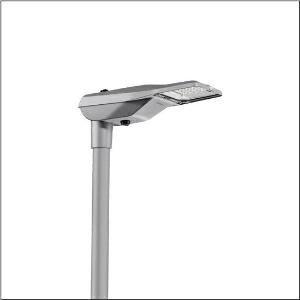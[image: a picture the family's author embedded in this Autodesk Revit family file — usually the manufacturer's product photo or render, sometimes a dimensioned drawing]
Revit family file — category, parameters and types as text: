
# Revit family: streetlight_sl_21_micro___st1_5a_5xe1p43t08db_e62a
name_source: partatom
category: Lighting Fixtures
units: mm (PartAtom-declared; Revit-internal decimal feet)

## family parameters
Cut with Voids When Loaded = No
Host = Face
Light Source = No
Part Type = Normal
Room Calculation Point = No
Round Connector Dimension = Use Diameter
Shared = No

## types (1)
- --- (1 x LED, 5230 lm, 39.1 W, 4000K)
    Apparent Load = 39 VA
    CIE Flux Codes = 22 53 95 100 100
    Color Rendering = 70
    Color Temperature = 4000K
    Default Elevation = 1800 mm
    Description = Streetlight SL 21 micro, mast luminaire, primary light control with lens, of PMMA, primary optical cover: cover, of toughened safety glass, transparent, light distribution: ST1.5a, light emission: direct distribution, primary light characteristic: asymmetric, installation type: side-entry, post-top, LED, High Power LED, rated luminous flux: 5.230lm, luminous efficacy: 134lm/W, light colour: 740, colour temperature: 4000K, control: flexible luminous flux parameterisation, time-dependent luminous flux control, constant luminous flux control, overheat protection, presetting dimming logarithmic, mains connection: 220..240V, AC, 50/60Hz, start of lifetime: 39W, end of service life: 41W, reduction: 18W, luminaire housing, of diecast aluminium, powder-coated, Siteco® metallic grey (DB 702S), corrosivity category C5 mid according to DIN EN ISO 12944, please order mast flange separately, inclination adjustable: 0°, 5°, 10°, 15°, sealing non-destructively replaceable, multi-level sealing system, length: 528mm, width: 235mm, height: 110mm, mast flange for spigot size: 42mm (side-entry): 5XC10008XM4, 60/48mm (side-entry/post-top): 5XC10108XM2, 76/60mm (side-entry/post-top): 5XC10108XM1, Smart Interface below and above, protection rating (complete): IP66, insulation class (complete): insulation class II (safety insulation), certification: CE, ENEC, ENEC+, VDE, impact resistance: IK09, permissible operating ambient temperature for outdoor applications: -40..+50°C, standard-compliant lighting for roads and squares, packaging unit: 1 piece

Light Distribution: ST1.5a
    Height = 110 mm
    Lamp = 1 x LED
    Lamp Light Flux = 5230 lm
    Lamp Power = 39.1 W
    Lamp count = 1
    Length = 528 mm
    Luminous efficacy = 134 lm/W
    Manufacturer = Siteco
    ModVariant = No
    Model = 5XE1P43T08DB
    Number of Poles = 1
    OnlyDefault = Yes
    Power Factor = 1
    Product Name = Streetlight SL 21 micro | ST1.5a
    Product group = mast luminaire | pylon top
    ProductGroupID = 6100
    Protection Class = Protection class II
    Protection Degree = IP 66
    RLX_Detail_Level = 1
    RLX_Emergency_Light_Flux = 0 lm
    RLX_Emergency_Type = 0
    RLX_Emergency_Type_DB = No
    RlxData = <blob elided: 102437 chars, md5=ec911d0e>
    Socket = socket
    Standby Power = 0 W
    System Light Flux = 5230 lm
    System Power = 39 W
    Type Comments = factory setting: luminous flux: 100 % | dim-lin: 254 | 765 mA
    Type Image = l_1007239.jpg
    URL = http://relux.com
    VarID = @adj_103791
    Voltage = 0 V
    Weight = 0.00 kg
    Width = 235 mm

## geometry (parser evidence)
native form markers: Blend x4, Sweep x11
no freeform markers — native parametric forms only
